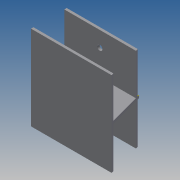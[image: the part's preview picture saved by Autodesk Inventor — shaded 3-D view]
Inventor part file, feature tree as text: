
AUTODESK INVENTOR PART (.ipt)
format: ipt  version: 2014 SP1 (Build 180222100, 222)  size: 135,168 bytes
history: native  units: in
note: dims shown in document units (in); Inventor stores cm internally (conversion verified against a paired STEP export)
features: sketch x6, extrude x5, plane x2, hole x1
ambient origin geometry x8: Origin, YZ Plane, XZ Plane, XY Plane, X Axis, Y Axis, Z Axis, Center Point
bodies: Solid1 (feature_tree)
feature tree (14):
  extrude  "Extrusion1"  Depth=0.12in
  plane  "Work Plane1"
  extrude  "Extrusion2"  Depth=0.12in
  extrude  "Extrusion3"  TaperAngle=90.0deg  [1 undecoded]
  extrude  "Extrusion4"  Depth=0.75in TaperAngle=0.0deg
  hole  "Hole1"  [1 undecoded]
  plane  "Work Plane2"
  extrude  "DRAWING_ONLY_ALIGN"  Depth=0.75in
  sketch  "Sketch2"  dims[d2=0.5in d3=0.12in]
  sketch  "Sketch3"  dims[d4=2.0in d5=0.12in]
  sketch  "Sketch4"  dims[d6=4.12in d7=90.0deg]
  sketch  "Sketch5"  dims[d9=0.75in d10=4.0in d11=0.0in]
  sketch  "Sketch6"  dims[d12=15.0deg d13=0.52in d14=0.0in]
  sketch  "Sketch7"  dims[d15=0.12in d16=0.75in d17=3.0in d18=1.5in d19=0.0in d20=1.0in d21=2.0in d22=0.0in d23=0.25in d24=0.25in d25=0.75in d26=0.75in d27=0.25in d28=0.75in d29=0.375in d30=0.25in d31=0.5635in d32=1.0in d33=0.8108in d34=-0.52in d35=0.12in d36=0.1in d37=0.3in d38=0.0in d39=0.0in]
note: 2 required parameter values undecoded (feature->parameter linkage not recoverable at this tier; creation-order binding heuristic only, values carry confidence <= 0.55)
